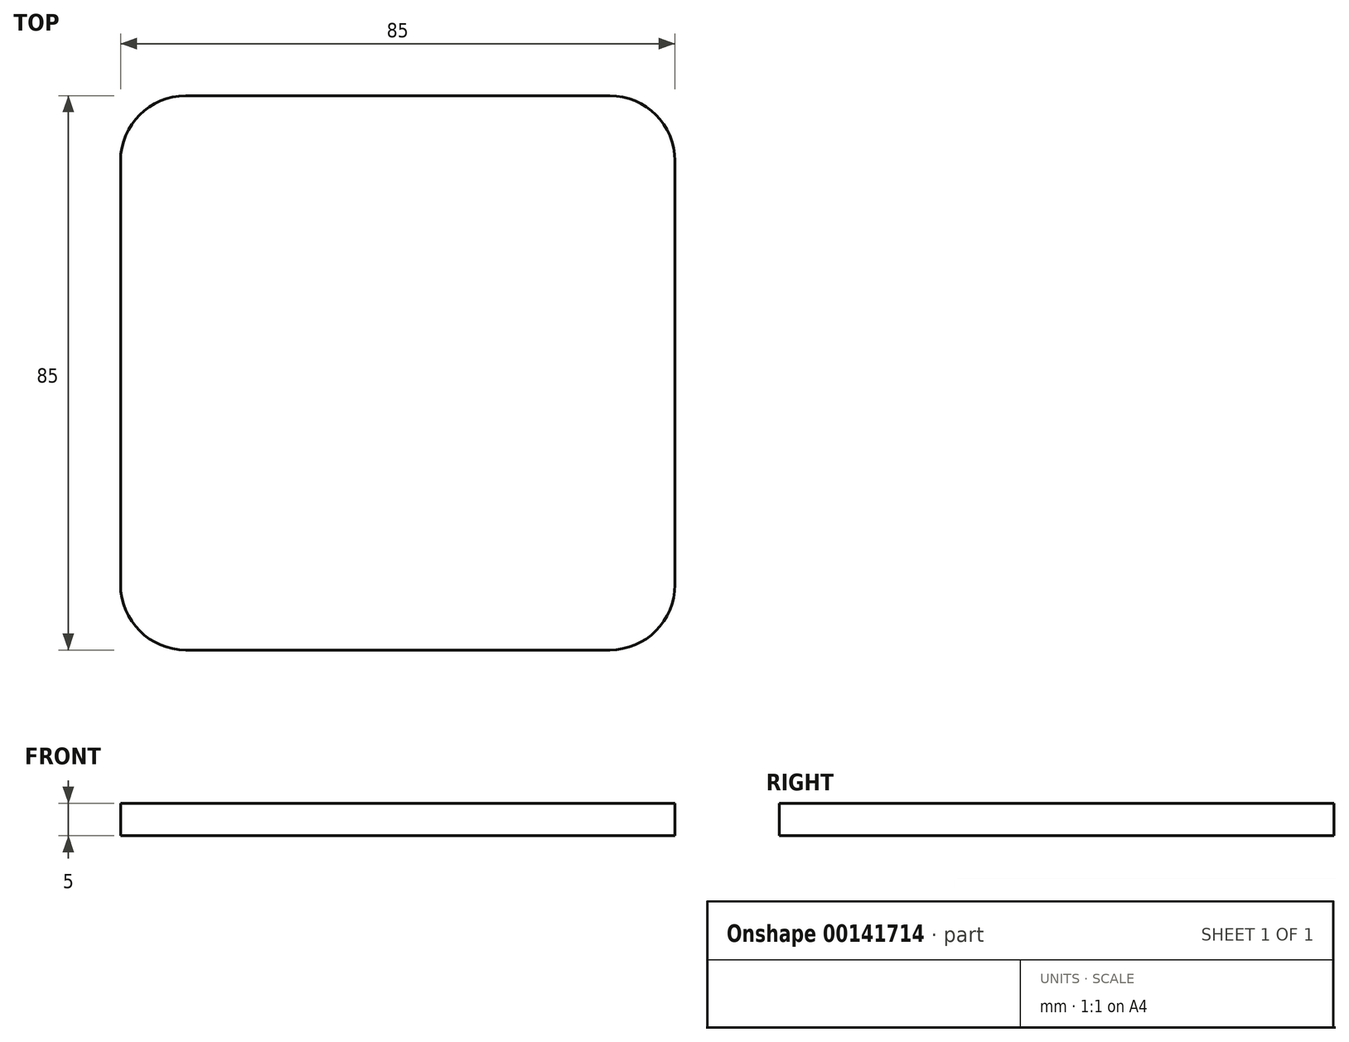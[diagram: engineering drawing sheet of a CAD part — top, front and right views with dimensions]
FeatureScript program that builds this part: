
annotation { "Feature Type Name" : "Feature", "Feature Type Description" : "" }
export const myFeature = defineFeature(function(context is Context, id is Id, definition is map)
    precondition{}
    {
        {
            var Q0;
            Q0=qCreatedBy(makeId("Top.planeOp"),FACE);
            var sketch = newSketch(context, id + "F0", { "sketchPlane" : qUnion([Q0])});
            skLineSegment(sketch, "E0.bottom", {"start": v(-32.5, 42.5) * mm, "end": v(32.5, 42.5) * mm});
            skLineSegment(sketch, "E0.top", {"start": v(-32.5, -42.5) * mm, "end": v(32.5, -42.5) * mm});
            skLineSegment(sketch, "E0.left", {"start": v(-42.5, 32.5) * mm, "end": v(-42.5, -32.5) * mm});
            skLineSegment(sketch, "E0.right", {"start": v(42.5, 32.5) * mm, "end": v(42.5, -32.5) * mm});
            skPoint(sketch, "E1.visualSharp", {"position": v(-42.5, 42.5) * mm});
            skArc(sketch, "E1.filletArc", {"start": v(-32.5, 42.5) * mm, "mid": v(-39.57, 39.57) * mm, "end": v(-42.5, 32.5) * mm});
            skPoint(sketch, "E2.visualSharp", {"position": v(42.5, 42.5) * mm});
            skArc(sketch, "E2.filletArc", {"start": v(42.5, 32.5) * mm, "mid": v(39.57, 39.57) * mm, "end": v(32.5, 42.5) * mm});
            skPoint(sketch, "E3.visualSharp", {"position": v(42.5, -42.5) * mm});
            skArc(sketch, "E3.filletArc", {"start": v(32.5, -42.5) * mm, "mid": v(39.57, -39.57) * mm, "end": v(42.5, -32.5) * mm});
            skPoint(sketch, "E4.visualSharp", {"position": v(-42.5, -42.5) * mm});
            skArc(sketch, "E4.filletArc", {"start": v(-42.5, -32.5) * mm, "mid": v(-39.57, -39.57) * mm, "end": v(-32.5, -42.5) * mm});
            skSolve(sketch);
        }
        {
            var Q0;
            Q0=qSketchRegion(id+"F0",true);
            extrude(context, id + "F1", {"entities" : qUnion([Q0]), "depth" : 5 * mm});
        }
    });
